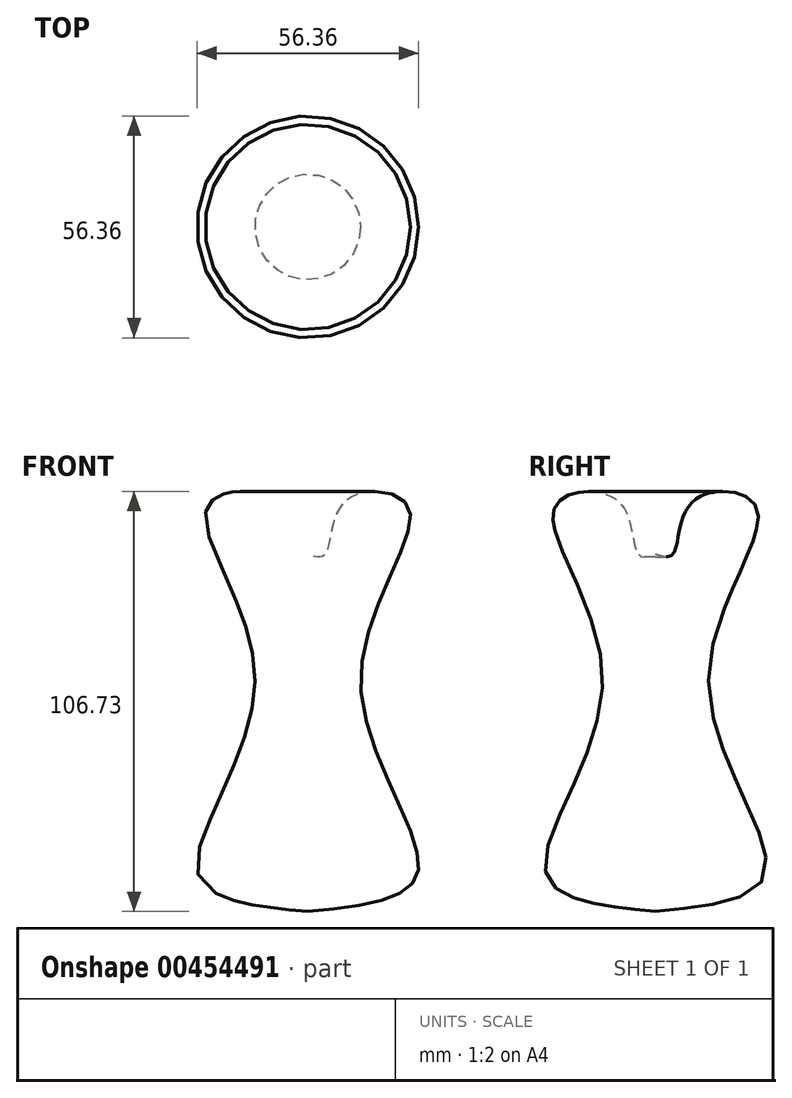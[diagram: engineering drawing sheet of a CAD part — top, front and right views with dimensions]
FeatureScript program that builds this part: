
annotation { "Feature Type Name" : "Feature", "Feature Type Description" : "" }
export const myFeature = defineFeature(function(context is Context, id is Id, definition is map)
    precondition{}
    {
        {
            var Q0;
            Q0=qCreatedBy(makeId("Front.planeOp"),FACE);
            var sketch = newSketch(context, id + "F0", { "sketchPlane" : qUnion([Q0])});
            skLineSegment(sketch, "E0", {"start": v(0, 55.35) * mm, "end": v(0, -48.45) * mm});
            skFitSpline(sketch, "E1", {"points": [v(0, -48.45) * mm, v(27.95, -38.65) * mm, v(13.43, 11.07) * mm, v(25.4, 54.62) * mm, v(9.44, 55.7) * mm, v(4.36, 42.28) * mm, v(0, 42.28) * mm], "startDerivative": vector(210.55, 19.94) * mm, "endDerivative": vector(-71.24, 23.91) * mm});
            skSolve(sketch);
        }
        {
            var Q0;
            {var subQ0=sQuery(id+"F0.wireOp",EDGE,"E1");Q0=makeQuery(id+"F0.imprint","IMPRINT",FACE,{"disambiguationData":[TD([[makeQuery(id+"F0.imprint","IMPRINT",EDGE,{"derivedFrom":subQ0}),1.0]])]});}
            var Q1;
            Q1=sQuery(id+"F0.wireOp",EDGE,"E0");
            revolve(context, id + "F1", {"entities" : qUnion([Q0]), "axis" : qUnion([Q1]), "revolveType" : RevolveType.FULL});
        }
    });
